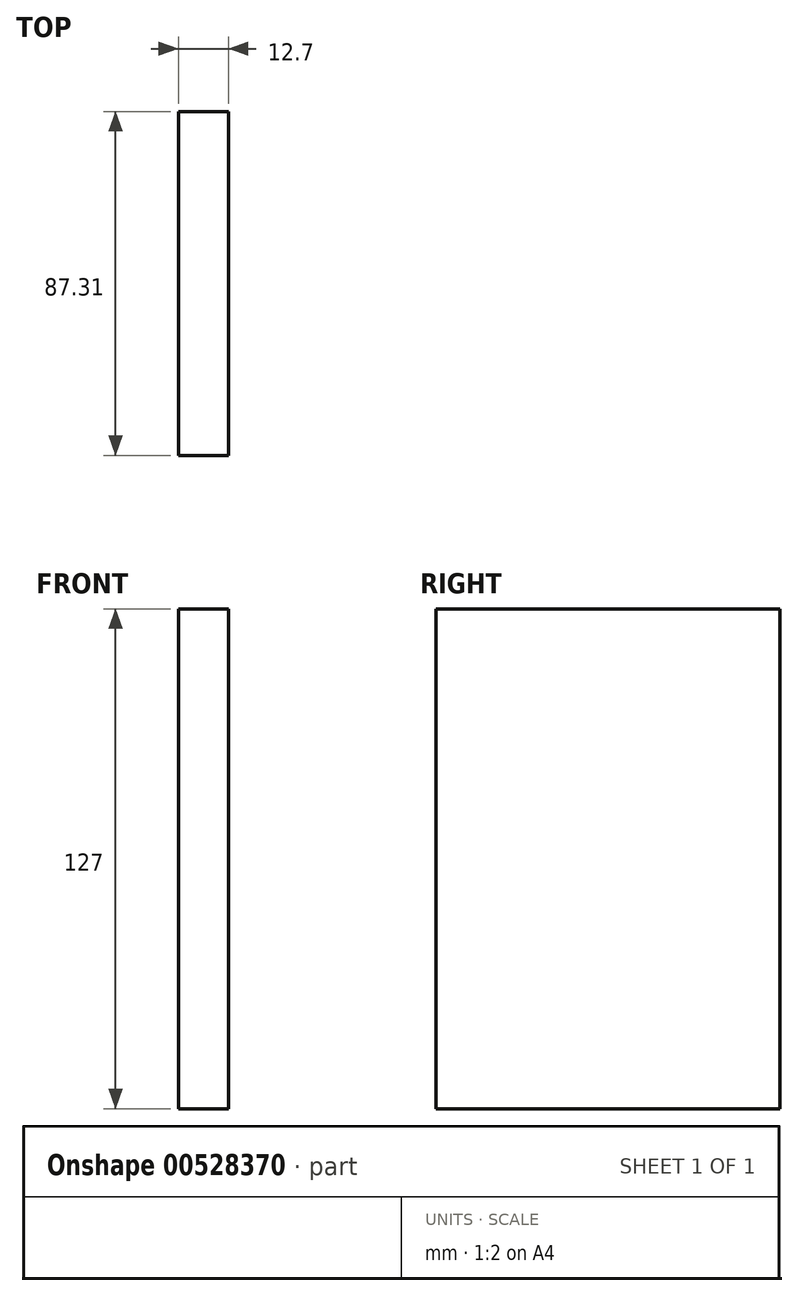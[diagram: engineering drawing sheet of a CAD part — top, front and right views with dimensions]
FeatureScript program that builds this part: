
annotation { "Feature Type Name" : "Feature", "Feature Type Description" : "" }
export const myFeature = defineFeature(function(context is Context, id is Id, definition is map)
    precondition{}
    {
        {
            var Q0;
            Q0=qCreatedBy(makeId("Front.planeOp"),FACE);
            var sketch = newSketch(context, id + "F0", { "sketchPlane" : qUnion([Q0])});
            skLineSegment(sketch, "E0.bottom", {"start": v(-6.35, -63.5) * mm, "end": v(6.35, -63.5) * mm});
            skLineSegment(sketch, "E0.top", {"start": v(-6.35, 63.5) * mm, "end": v(6.35, 63.5) * mm});
            skLineSegment(sketch, "E0.left", {"start": v(-6.35, -63.5) * mm, "end": v(-6.35, 63.5) * mm});
            skLineSegment(sketch, "E0.right", {"start": v(6.35, -63.5) * mm, "end": v(6.35, 63.5) * mm});
            skPoint(sketch, "E0.middle", {"position": v(0, 0) * mm});
            skSolve(sketch);
        }
        {
            var Q0;
            Q0=makeQuery(id+"F0.imprint","IMPRINT",FACE,{"disambiguationData":[TD([[makeQuery(id+"F0.imprint","IMPRINT",EDGE,{"derivedFrom":sQuery(id+"F0.wireOp",EDGE,"E0.bottom")}),1.0]])]});
            extrude(context, id + "F1", {"entities" : qUnion([Q0]), "depth" : 87.31 * mm, "offsetDistance" : 25.4 * mm});
        }
    });
